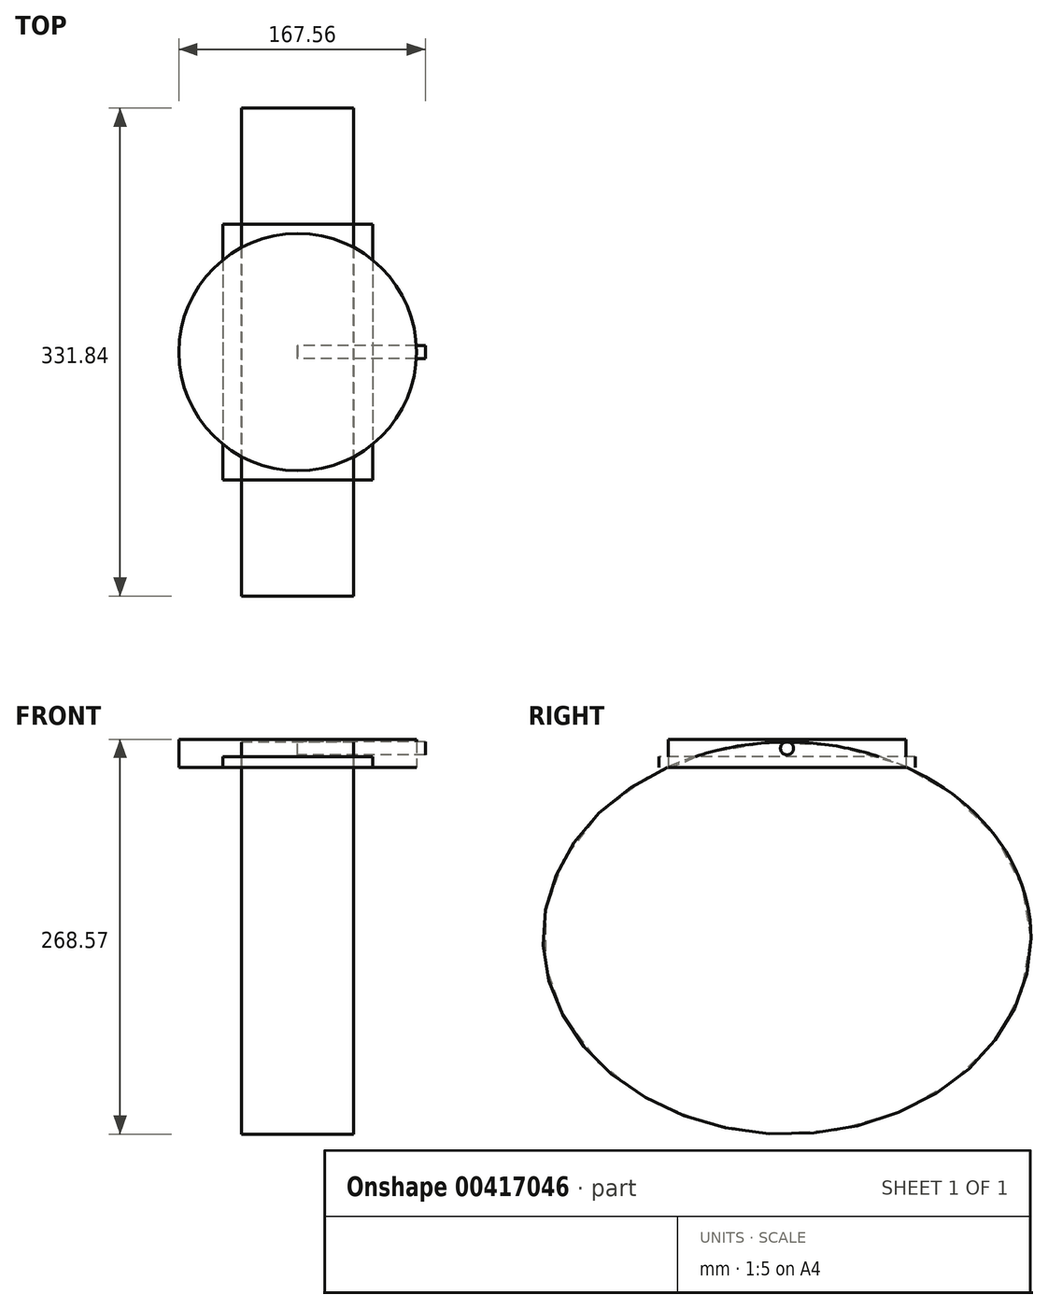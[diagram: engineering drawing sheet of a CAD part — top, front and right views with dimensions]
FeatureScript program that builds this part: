
annotation { "Feature Type Name" : "Feature", "Feature Type Description" : "" }
export const myFeature = defineFeature(function(context is Context, id is Id, definition is map)
    precondition{}
    {
        {
            var Q0;
            Q0=qCreatedBy(makeId("Top.planeOp"),FACE);
            var sketch = newSketch(context, id + "F0", { "sketchPlane" : qUnion([Q0])});
            skCircle(sketch, "E0", {"center": v(0, 0) * mm, "radius": 80.77 * mm});
            skSolve(sketch);
        }
        {
            var Q0;
            Q0 = qSketchRegion(id + "F0", true);
            var sketch = newSketch(context, id + "F1", { "sketchPlane" : qUnion([Q0])});
            skLineSegment(sketch, "E1.bottom", {"start": v(50.96, 87.1) * mm, "end": v(-50.96, 87.1) * mm});
            skLineSegment(sketch, "E1.top", {"start": v(50.96, -87.1) * mm, "end": v(-50.96, -87.1) * mm});
            skLineSegment(sketch, "E1.left", {"start": v(50.96, 87.1) * mm, "end": v(50.96, -87.1) * mm});
            skLineSegment(sketch, "E1.right", {"start": v(-50.96, 87.1) * mm, "end": v(-50.96, -87.1) * mm});
            skPoint(sketch, "E1.middle", {"position": v(0, 0) * mm});
            skSolve(sketch);
        }
        {
            var Q0;
            Q0 = qSketchRegion(id + "F1", true);
            extrude(context, id + "F2", {"entities" : qUnion([Q0]), "depth" : 7.37 * mm});
        }
        {
            var Q0;
            Q0=makeQuery(id+"F0.imprint","IMPRINT",FACE,{"disambiguationData":[TD([[makeQuery(id+"F0.imprint","IMPRINT",EDGE,{"derivedFrom":sQuery(id+"F0.wireOp",EDGE,"E0")}),1.0]])]});
            var Q1;
            Q1=sQuery(id+"F0.wireOp",EDGE,"E0");
            extrude(context, id + "F3", {"entities" : qUnion([Q0]), "surfaceEntities" : qUnion([Q1]), "depth" : 19.05 * mm});
        }
        {
            var Q0;
            Q0=qCreatedBy(makeId("Right.planeOp"),FACE);
            var sketch = newSketch(context, id + "F4", { "sketchPlane" : qUnion([Q0])});
            skEllipse(sketch, "E2", {"center": v(0, -116.18) * mm, "majorRadius": 165.92 * mm, "minorRadius": 133.34 * mm, "majorAxis": v(1, 0)});
            skLineSegment(sketch, "E3", {"start": v(80.77, 19.05) * mm, "end": v(80.77, 0) * mm});
            skLineSegment(sketch, "E4", {"start": v(-80.77, 0) * mm, "end": v(-80.77, 19.05) * mm});
            skFitSpline(sketch, "E5.0", {"points": [v(153.19, -119.1) * mm, v(153.23, -116.18) * mm, v(153.19, -113.26) * mm, v(153, -109.38) * mm, v(152.56, -104.56) * mm, v(151.67, -98.8) * mm, v(150.02, -91.2) * mm, v(147.1, -81.85) * mm, v(142.22, -70.91) * mm, v(136.01, -60.35) * mm, v(129.74, -51.91) * mm, v(124.07, -45.43) * mm, v(119.5, -40.72) * mm, v(115.43, -36.92) * mm, v(112.02, -33.96) * mm, v(109.38, -31.79) * mm, v(106.67, -29.66) * mm, v(102.97, -26.9) * mm, v(98.2, -23.6) * mm, v(92.25, -19.88) * mm, v(84.03, -15.24) * mm, v(73.24, -10.05) * mm, v(59.58, -4.86) * mm, v(45.32, -0.76) * mm, v(33.03, 1.73) * mm, v(23, 3.13) * mm, v(15.4, 3.9) * mm, v(9, 4.28) * mm, v(3.87, 4.43) * mm, v(0, 4.47) * mm, v(-3.87, 4.43) * mm, v(-9, 4.28) * mm, v(-15.4, 3.9) * mm, v(-23, 3.13) * mm, v(-33.03, 1.73) * mm, v(-45.32, -0.76) * mm, v(-59.58, -4.86) * mm, v(-73.24, -10.05) * mm, v(-84.03, -15.24) * mm, v(-92.25, -19.88) * mm, v(-98.2, -23.6) * mm, v(-102.97, -26.9) * mm, v(-106.67, -29.66) * mm, v(-109.38, -31.79) * mm, v(-112.02, -33.96) * mm, v(-115.43, -36.92) * mm, v(-119.5, -40.72) * mm, v(-124.07, -45.43) * mm, v(-129.74, -51.91) * mm, v(-136.01, -60.35) * mm, v(-142.22, -70.91) * mm, v(-147.1, -81.85) * mm, v(-150.02, -91.2) * mm, v(-151.67, -98.8) * mm, v(-152.56, -104.56) * mm, v(-153, -109.38) * mm, v(-153.19, -113.26) * mm, v(-153.23, -116.18) * mm, v(-153.19, -119.1) * mm, v(-153, -122.99) * mm, v(-152.56, -127.81) * mm, v(-151.67, -133.56) * mm, v(-150.02, -141.16) * mm, v(-147.1, -150.52) * mm, v(-142.22, -161.45) * mm, v(-136.01, -172.02) * mm, v(-129.74, -180.45) * mm, v(-124.07, -186.93) * mm, v(-119.5, -191.65) * mm, v(-115.43, -195.45) * mm, v(-112.02, -198.4) * mm, v(-109.38, -200.58) * mm, v(-106.67, -202.7) * mm, v(-102.97, -205.46) * mm, v(-98.2, -208.76) * mm, v(-92.25, -212.49) * mm, v(-84.03, -217.13) * mm, v(-73.24, -222.32) * mm, v(-59.58, -227.5) * mm, v(-45.32, -231.61) * mm, v(-33.03, -234.1) * mm, v(-23, -235.5) * mm, v(-15.4, -236.26) * mm, v(-9, -236.65) * mm, v(-3.87, -236.8) * mm, v(0, -236.84) * mm, v(3.87, -236.8) * mm, v(9, -236.65) * mm, v(15.4, -236.26) * mm, v(23, -235.5) * mm, v(33.03, -234.1) * mm, v(45.32, -231.61) * mm, v(59.58, -227.5) * mm, v(73.24, -222.32) * mm, v(84.03, -217.13) * mm, v(92.25, -212.49) * mm, v(98.2, -208.76) * mm, v(102.97, -205.46) * mm, v(106.67, -202.7) * mm, v(109.38, -200.58) * mm, v(112.02, -198.4) * mm, v(115.43, -195.45) * mm, v(119.5, -191.65) * mm, v(124.07, -186.93) * mm, v(129.74, -180.45) * mm, v(136.01, -172.02) * mm, v(142.22, -161.45) * mm, v(147.1, -150.52) * mm, v(150.02, -141.16) * mm, v(151.67, -133.56) * mm, v(152.56, -127.81) * mm, v(153, -122.99) * mm, v(153.19, -119.1) * mm, v(153.23, -116.18) * mm, v(153.19, -113.26) * mm, v(153.19, -119.1) * mm]});
            skSolve(sketch);
        }
        {
            var Q0;
            Q0=makeQuery(id+"F4.imprint","IMPRINT",FACE,{"disambiguationData":[TD([[makeQuery(id+"F4.imprint","IMPRINT",EDGE,{"derivedFrom":sQuery(id+"F4.wireOp",EDGE,"E2")}),1.0]])]});
            extrude(context, id + "F5", {"entities" : qUnion([Q0]), "endBound" : BoundingType.SYMMETRIC, "depth" : 76.2 * mm});
        }
        {
            var Q0;
            Q0=qCreatedBy(makeId("Right.planeOp"),FACE);
            var sketch = newSketch(context, id + "F6", { "sketchPlane" : qUnion([Q0])});
            skCircle(sketch, "E6", {"center": v(0, 12.94) * mm, "radius": 4.43 * mm});
            skSolve(sketch);
        }
        {
            var Q0;
            Q0 = qSketchRegion(id + "F6", true);
            extrude(context, id + "F7", {"entities" : qUnion([Q0]), "depth" : 86.8 * mm});
        }
    });
